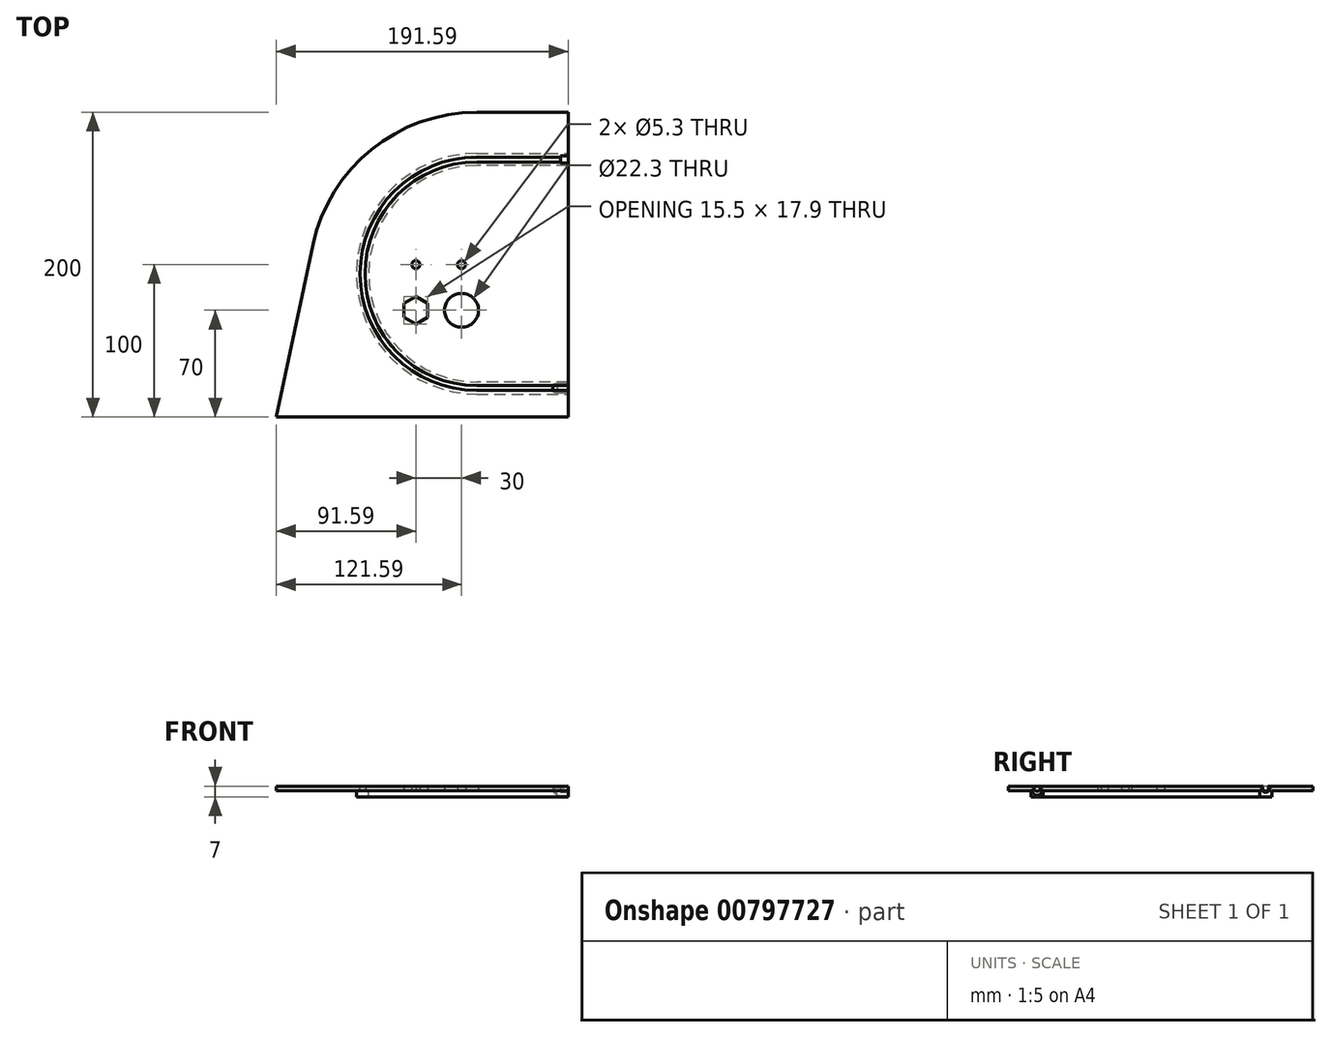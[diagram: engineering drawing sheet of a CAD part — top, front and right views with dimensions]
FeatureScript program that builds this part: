
annotation { "Feature Type Name" : "Feature", "Feature Type Description" : "" }
export const myFeature = defineFeature(function(context is Context, id is Id, definition is map)
    precondition{}
    {
        {
            var Q0;
            Q0=qCreatedBy(makeId("Top.planeOp"),FACE);
            var sketch = newSketch(context, id + "F0", { "sketchPlane" : qUnion([Q0])});
            skLineSegment(sketch, "E0", {"start": v(-191.59, 0) * mm, "end": v(-167.6, 112.87) * mm});
            skLineSegment(sketch, "E1", {"start": v(0, 200) * mm, "end": v(-60, 200) * mm});
            skLineSegment(sketch, "E2", {"start": v(0, 200) * mm, "end": v(0, 0) * mm});
            skLineSegment(sketch, "E3", {"start": v(0, 0) * mm, "end": v(-191.59, 0) * mm});
            skArc(sketch, "E4", {"start": v(-60, 200) * mm, "mid": v(-129.23, 175.49) * mm, "end": v(-167.6, 112.87) * mm});
            skSolve(sketch);
        }
        {
            var Q0;
            Q0=makeQuery(id+"F0.imprint","IMPRINT",FACE,{"disambiguationData":[TD([[makeQuery(id+"F0.imprint","IMPRINT",EDGE,{"derivedFrom":sQuery(id+"F0.wireOp",EDGE,"E0")}),-1.0]])]});
            var sketch = newSketch(context, id + "F1", { "sketchPlane" : qUnion([Q0])});
            skCircle(sketch, "E5.cCircle", {"center": v(-100, 70) * mm, "radius": 8.95 * mm, "construction": true});
            skLineSegment(sketch, "E5.0", {"start": v(-107.75, 74.47) * mm, "end": v(-100, 78.95) * mm});
            skLineSegment(sketch, "E5.1", {"start": v(-100, 78.95) * mm, "end": v(-92.25, 74.47) * mm});
            skLineSegment(sketch, "E5.2", {"start": v(-92.25, 74.47) * mm, "end": v(-92.25, 65.53) * mm});
            skLineSegment(sketch, "E5.3", {"start": v(-92.25, 65.53) * mm, "end": v(-100, 61.05) * mm});
            skLineSegment(sketch, "E5.4", {"start": v(-100, 61.05) * mm, "end": v(-107.75, 65.53) * mm});
            skLineSegment(sketch, "E5.5", {"start": v(-107.75, 65.53) * mm, "end": v(-107.75, 74.47) * mm});
            skCircle(sketch, "E6", {"center": v(-70, 70) * mm, "radius": 11.15 * mm});
            skCircle(sketch, "E7", {"center": v(-70, 100) * mm, "radius": 2.65 * mm});
            skCircle(sketch, "E8", {"center": v(-100, 100) * mm, "radius": 2.65 * mm});
            skSolve(sketch);
        }
        {
            var Q0;
            Q0 = qSketchRegion(id + "F0", true);
            extrude(context, id + "F2", {"entities" : qUnion([Q0]), "depth" : 3 * mm, "offsetDistance" : 25 * mm});
        }
        {
            var Q0;
            Q0 = qSketchRegion(id + "F1", true);
            extrude(context, id + "F3", {"entities" : qUnion([Q0]), "operationType" : NewBodyOperationType.REMOVE, "depth" : 25 * mm, "offsetDistance" : 25 * mm});
        }
        {
            var Q0;
            Q0=makeQuery(id+"F2.opExtrude","CAP_FACE",FACE,{"disambiguationData":[OSD([sQuery(id+"F0.wireOp",EDGE,"E0"),sQuery(id+"F0.wireOp",EDGE,"E1"),sQuery(id+"F0.wireOp",EDGE,"E2"),sQuery(id+"F0.wireOp",EDGE,"E3"),sQuery(id+"F0.wireOp",EDGE,"E4")])],"isStart":true});
            var sketch = newSketch(context, id + "F4", { "sketchPlane" : qUnion([Q0])});
            skArc(sketch, "E9", {"start": v(-60, -15) * mm, "mid": v(-139, -94) * mm, "end": v(-60, -173) * mm});
            skLineSegment(sketch, "E10", {"start": v(-60, -15) * mm, "end": v(0, -15) * mm});
            skLineSegment(sketch, "E11", {"start": v(0, -15) * mm, "end": v(0, -23) * mm});
            skLineSegment(sketch, "E12", {"start": v(0, -23) * mm, "end": v(-60, -23) * mm});
            skLineSegment(sketch, "E13", {"start": v(-60, -173) * mm, "end": v(0, -173) * mm});
            skLineSegment(sketch, "E14", {"start": v(0, -173) * mm, "end": v(0, -165) * mm});
            skLineSegment(sketch, "E15", {"start": v(0, -165) * mm, "end": v(-60, -165) * mm});
            skArc(sketch, "E16", {"start": v(-60, -23) * mm, "mid": v(-131, -94) * mm, "end": v(-60, -165) * mm});
            skSolve(sketch);
        }
        {
            var Q0;
            Q0 = qSketchRegion(id + "F4", true);
            extrude(context, id + "F5", {"entities" : qUnion([Q0]), "operationType" : NewBodyOperationType.ADD, "depth" : 4 * mm, "offsetDistance" : 25 * mm});
        }
        {
            var Q0;
            Q0=makeQuery(id+"F5.opExtrude","CAP_FACE",FACE,{"disambiguationData":[OSD([sQuery(id+"F4.wireOp",EDGE,"E9"),sQuery(id+"F4.wireOp",EDGE,"E10"),sQuery(id+"F4.wireOp",EDGE,"E11"),sQuery(id+"F4.wireOp",EDGE,"E12"),sQuery(id+"F4.wireOp",EDGE,"E13"),sQuery(id+"F4.wireOp",EDGE,"E14"),sQuery(id+"F4.wireOp",EDGE,"E15"),sQuery(id+"F4.wireOp",EDGE,"E16")])],"isStart":false});
            var sketch = newSketch(context, id + "F6", { "sketchPlane" : qUnion([Q0])});
            skLineSegment(sketch, "E17", {"start": v(0, -19) * mm, "end": v(-60, -19) * mm});
            skLineSegment(sketch, "E18", {"start": v(0, -169) * mm, "end": v(-60, -169) * mm});
            skArc(sketch, "E19", {"start": v(-60, -19) * mm, "mid": v(-135, -94) * mm, "end": v(-60, -169) * mm});
            skSolve(sketch);
        }
        {
            var Q0;
            Q0=makeQuery(id+"F5.boolean.opBoolean","MERGE",FACE,{"derivedFrom":[makeQuery(id+"F2.opExtrude","SWEPT_FACE",FACE,{"disambiguationData":[OSD([sQuery(id+"F0.wireOp",EDGE,"E2")])]}),makeQuery(id+"F5.opExtrude","SWEPT_FACE",FACE,{"disambiguationData":[OSD([sQuery(id+"F4.wireOp",EDGE,"E11")])]}),makeQuery(id+"F5.opExtrude","SWEPT_FACE",FACE,{"disambiguationData":[OSD([sQuery(id+"F4.wireOp",EDGE,"E14")])]})]});
            var sketch = newSketch(context, id + "F7", { "sketchPlane" : qUnion([Q0])});
            skCircle(sketch, "E20", {"center": v(19, 1.8) * mm, "radius": 2 * mm});
            skPoint(sketch, "E20.centerSnap0", {"position": v(19, -4) * mm});
            skSolve(sketch);
        }
        {
            var Q0;
            Q0 = qSketchRegion(id + "F7", true);
            var Q1;
            Q1 = qConstructionFilter(qBodyType(qCreatedBy(id + "F6" ,EDGE), BodyType.WIRE), ConstructionObject.NO);
            sweep(context, id + "F8", {"operationType" : NewBodyOperationType.REMOVE, "profiles" : qUnion([Q0]), "path" : qUnion([Q1])});
        }
        {
            var Q0;
            Q0=makeQuery(id+"F5.boolean.opBoolean","MERGE",FACE,{"derivedFrom":[makeQuery(id+"F2.opExtrude","SWEPT_FACE",FACE,{"disambiguationData":[OSD([sQuery(id+"F0.wireOp",EDGE,"E2")])]}),makeQuery(id+"F5.opExtrude","SWEPT_FACE",FACE,{"disambiguationData":[OSD([sQuery(id+"F4.wireOp",EDGE,"E11")])]}),makeQuery(id+"F5.opExtrude","SWEPT_FACE",FACE,{"disambiguationData":[OSD([sQuery(id+"F4.wireOp",EDGE,"E14")])]})]});
            var sketch = newSketch(context, id + "F9", { "sketchPlane" : qUnion([Q0])});
            skCircle(sketch, "E21", {"center": v(19, 0) * mm, "radius": 3 * mm});
            skPoint(sketch, "E21.centerSnap0", {"position": v(19, -0.2) * mm});
            skCircle(sketch, "E22", {"center": v(169, 1.8) * mm, "radius": 2.75 * mm});
            skSolve(sketch);
        }
        {
            var Q0;
            Q0 = qSketchRegion(id + "F9", true);
            extrude(context, id + "F10", {"entities" : qUnion([Q0]), "operationType" : NewBodyOperationType.REMOVE, "oppositeDirection" : true, "depth" : 5 * mm, "offsetDistance" : 25 * mm});
        }
        {
            var Q0;
            Q0=makeQuery(id+"F10.boolean.opBoolean","INTERSECT",EDGE,{"derivedFrom":[makeQuery(id+"F8.boolean.opBoolean","COPY",FACE,{"derivedFrom":makeQuery(id+"F8.opSweep","SWEPT_FACE",FACE,{"disambiguationData":[OSD([sQuery(id+"F6.wireOp",EDGE,"E17"),sQuery(id+"F7.wireOp",EDGE,"E20")])]})}),makeQuery(id+"F10.opExtrude","CAP_FACE",FACE,{"disambiguationData":[OSD([sQuery(id+"F9.wireOp",EDGE,"E21")])],"isStart":false})]});
            chamfer(context, id + "F11", {"entities" : qUnion([Q0]), "width" : 5 * mm, "tangentPropagation" : true});
        }
    });
